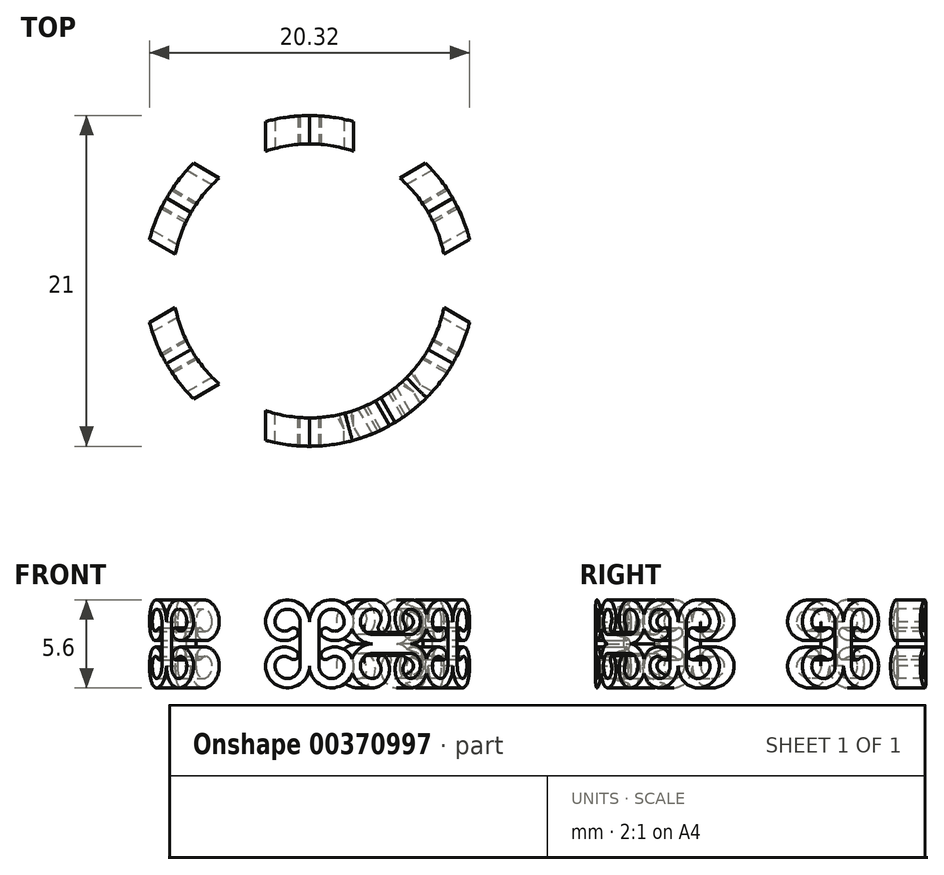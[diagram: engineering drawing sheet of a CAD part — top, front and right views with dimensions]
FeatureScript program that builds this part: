
annotation { "Feature Type Name" : "Feature", "Feature Type Description" : "" }
export const myFeature = defineFeature(function(context is Context, id is Id, definition is map)
    precondition{}
    {
        {
            var Q0;
            Q0=qCreatedBy(makeId("Front.planeOp"),FACE);
            var sketch = newSketch(context, id + "F0", { "sketchPlane" : qUnion([Q0])});
            skLineSegment(sketch, "E0.bottom", {"start": v(0, 0) * mm, "end": v(-2.8, 0) * mm, "construction": true});
            skLineSegment(sketch, "E0.top", {"start": v(0, 2.8) * mm, "end": v(-2.8, 2.8) * mm, "construction": true});
            skLineSegment(sketch, "E0.left", {"start": v(0, 0) * mm, "end": v(0, 2.8) * mm, "construction": true});
            skLineSegment(sketch, "E0.right", {"start": v(-2.8, 0) * mm, "end": v(-2.8, 2.8) * mm, "construction": true});
            skArc(sketch, "E1", {"start": v(0, 1.4) * mm, "mid": v(-1.4, 2.8) * mm, "end": v(-2.8, 1.4) * mm});
            skArc(sketch, "E2", {"start": v(-2.8, 1.4) * mm, "mid": v(-2.1, 0.31) * mm, "end": v(-0.83, 0.48) * mm});
            skLineSegment(sketch, "E3", {"start": v(-1.6, 1.4) * mm, "end": v(-0.83, 0.48) * mm, "construction": true});
            skLineSegment(sketch, "E4", {"start": v(-1.6, 1.4) * mm, "end": v(-1.6, 0.2) * mm, "construction": true});
            skArc(sketch, "E5.0", {"start": v(-2.2, 1.4) * mm, "mid": v(-1.85, 0.86) * mm, "end": v(-1.21, 0.94) * mm});
            skArc(sketch, "E5.1", {"start": v(-0.6, 1.4) * mm, "mid": v(-1.4, 2.2) * mm, "end": v(-2.2, 1.4) * mm});
            skArc(sketch, "E6", {"start": v(-0.83, 0.48) * mm, "mid": v(-0.8, 0.9) * mm, "end": v(-1.21, 0.94) * mm});
            skLineSegment(sketch, "E7", {"start": v(-0.6, 1.4) * mm, "end": v(-0.6, 0) * mm});
            skLineSegment(sketch, "E8", {"start": v(-0.6, 0) * mm, "end": v(0, 0) * mm});
            skLineSegment(sketch, "E9", {"start": v(0, 1.4) * mm, "end": v(0, 0) * mm});
            skLineSegment(sketch, "E10", {"start": v(-0.6, 1.4) * mm, "end": v(0, 1.4) * mm, "construction": true});
            skCircle(sketch, "E11", {"center": v(0, 0) * mm, "radius": 3.33 * mm, "construction": true});
            skSolve(sketch);
        }
        {
            var Q0;
            Q0=makeQuery(id+"F0.imprint","IMPRINT",FACE,{"disambiguationData":[TD([[makeQuery(id+"F0.imprint","IMPRINT",EDGE,{"derivedFrom":sQuery(id+"F0.wireOp",EDGE,"E1")}),1.0]])]});
            extrude(context, id + "F1", {"entities" : qUnion([Q0]), "endBound" : BoundingType.SYMMETRIC, "depth" : 8 * mm});
        }
        {
            var Q0;
            Q0=makeQuery(id+"F1.opExtrude","SWEPT_BODY",BODY,{"disambiguationData":[OSD([sQuery(id+"F0.wireOp",EDGE,"E1"),sQuery(id+"F0.wireOp",EDGE,"E2"),sQuery(id+"F0.wireOp",EDGE,"E5.0"),sQuery(id+"F0.wireOp",EDGE,"E5.1"),sQuery(id+"F0.wireOp",EDGE,"E6"),sQuery(id+"F0.wireOp",EDGE,"E7"),sQuery(id+"F0.wireOp",EDGE,"E8"),sQuery(id+"F0.wireOp",EDGE,"E9")])]});
            var Q1;
            Q1=makeQuery(id+"F1.opExtrude","SWEPT_FACE",FACE,{"disambiguationData":[OSD([sQuery(id+"F0.wireOp",EDGE,"E8")])]});
            mirror(context, id + "F2", {"operationType" : NewBodyOperationType.ADD, "entities" : qUnion([Q0]), "mirrorPlane" : qUnion([Q1])});
        }
        {
            var Q0;
            Q0=makeQuery(id+"F1.opExtrude","SWEPT_BODY",BODY,{"disambiguationData":[OSD([sQuery(id+"F0.wireOp",EDGE,"E1"),sQuery(id+"F0.wireOp",EDGE,"E2"),sQuery(id+"F0.wireOp",EDGE,"E5.0"),sQuery(id+"F0.wireOp",EDGE,"E5.1"),sQuery(id+"F0.wireOp",EDGE,"E6"),sQuery(id+"F0.wireOp",EDGE,"E7"),sQuery(id+"F0.wireOp",EDGE,"E8"),sQuery(id+"F0.wireOp",EDGE,"E9")])]});
            var Q1;
            {var subQ0=makeQuery(id+"F1.opExtrude","SWEPT_FACE",FACE,{"disambiguationData":[OSD([sQuery(id+"F0.wireOp",EDGE,"E9")])]});Q1=makeQuery(id+"F2.boolean.opBoolean","MERGE",FACE,{"derivedFrom":[subQ0,makeQuery(id+"F2.opPattern","COPY",FACE,{"derivedFrom":subQ0,"instanceName":"1"})]});}
            mirror(context, id + "F3", {"operationType" : NewBodyOperationType.ADD, "entities" : qUnion([Q0]), "mirrorPlane" : qUnion([Q1])});
        }
        {
            var Q0;
            Q0=qCreatedBy(makeId("Top.planeOp"),FACE);
            var sketch = newSketch(context, id + "F4", { "sketchPlane" : qUnion([Q0])});
            skCircle(sketch, "E12", {"center": v(0, 8.7) * mm, "radius": 8.7 * mm, "construction": true});
            skSolve(sketch);
        }
        {
            var Q0;
            Q0=makeQuery(id+"F1.opExtrude","SWEPT_BODY",BODY,{"disambiguationData":[OSD([sQuery(id+"F0.wireOp",EDGE,"E1"),sQuery(id+"F0.wireOp",EDGE,"E2"),sQuery(id+"F0.wireOp",EDGE,"E5.0"),sQuery(id+"F0.wireOp",EDGE,"E5.1"),sQuery(id+"F0.wireOp",EDGE,"E6"),sQuery(id+"F0.wireOp",EDGE,"E7"),sQuery(id+"F0.wireOp",EDGE,"E8"),sQuery(id+"F0.wireOp",EDGE,"E9")])]});
            var Q1;
            Q1=sQuery(id+"F0.wireOp",EDGE,"E11");
            transform(context, id + "F5", {"entities" : qUnion([Q0]), "transformType" : TransformType.ROTATION, "transformAxis" : qUnion([Q1]), "angle" : 90 * degree, "makeCopy" : true});
        }
        {
            var Q0;
            Q0=makeQuery(id+"F5.opPattern","COPY",BODY,{"derivedFrom":makeQuery(id+"F1.opExtrude","SWEPT_BODY",BODY,{"disambiguationData":[OSD([sQuery(id+"F0.wireOp",EDGE,"E1"),sQuery(id+"F0.wireOp",EDGE,"E2"),sQuery(id+"F0.wireOp",EDGE,"E5.0"),sQuery(id+"F0.wireOp",EDGE,"E5.1"),sQuery(id+"F0.wireOp",EDGE,"E6"),sQuery(id+"F0.wireOp",EDGE,"E7"),sQuery(id+"F0.wireOp",EDGE,"E8"),sQuery(id+"F0.wireOp",EDGE,"E9")])]}),"instanceName":"1"});
            var Q1;
            Q1=sQuery(id+"F4.wireOp",EDGE,"E12");
            transform(context, id + "F6", {"entities" : qUnion([Q0]), "transformType" : TransformType.ROTATION, "transformAxis" : qUnion([Q1]), "angle" : 30 * degree, "makeCopy" : false});
        }
        {
            var Q0;
            Q0=qCreatedBy(makeId("Top.planeOp"),FACE);
            var sketch = newSketch(context, id + "F7", { "sketchPlane" : qUnion([Q0])});
            skCircle(sketch, "E13.0", {"center": v(0, 8.7) * mm, "radius": 8.7 * mm});
            skCircle(sketch, "E14", {"center": v(0, 8.7) * mm, "radius": 10.5 * mm});
            skCircle(sketch, "E15", {"center": v(0, 8.7) * mm, "radius": 50 * mm});
            skSolve(sketch);
        }
        {
            var Q0;
            Q0=makeQuery(id+"F7.imprint","IMPRINT",FACE,{"disambiguationData":[TD([[makeQuery(id+"F7.imprint","IMPRINT",EDGE,{"derivedFrom":sQuery(id+"F7.wireOp",EDGE,"E14")}),-1.0]])]});
            var Q1;
            Q1=makeQuery(id+"F7.imprint","IMPRINT",FACE,{"disambiguationData":[TD([[makeQuery(id+"F7.imprint","IMPRINT",EDGE,{"derivedFrom":sQuery(id+"F7.wireOp",EDGE,"E13.0")}),1.0]])]});
            var Q2;
            Q2=makeQuery(id+"F7.imprint","IMPRINT",FACE,{"disambiguationData":[TD([[makeQuery(id+"F7.imprint","IMPRINT",EDGE,{"derivedFrom":sQuery(id+"F7.wireOp",EDGE,"E13.0")}),1.0]])]});
            extrude(context, id + "F8", {"entities" : qUnion([Q0, Q1, Q2]), "operationType" : NewBodyOperationType.REMOVE, "endBound" : BoundingType.SYMMETRIC, "oppositeDirection" : true, "depth" : 50 * mm});
        }
        {
            var Q0;
            Q0=makeQuery(id+"F1.opExtrude","SWEPT_BODY",BODY,{"disambiguationData":[OSD([sQuery(id+"F0.wireOp",EDGE,"E1"),sQuery(id+"F0.wireOp",EDGE,"E2"),sQuery(id+"F0.wireOp",EDGE,"E5.0"),sQuery(id+"F0.wireOp",EDGE,"E5.1"),sQuery(id+"F0.wireOp",EDGE,"E6"),sQuery(id+"F0.wireOp",EDGE,"E7"),sQuery(id+"F0.wireOp",EDGE,"E8"),sQuery(id+"F0.wireOp",EDGE,"E9")])]});
            var Q1;
            Q1=sQuery(id+"F4.wireOp",EDGE,"E12");
            circularPattern(context, id + "F9", {"operationType" : NewBodyOperationType.ADD, "entities" : qUnion([Q0]), "axis" : qUnion([Q1]), "angle" : 360 * degree, "instanceCount" : 6, "equalSpace" : true});
        }
    });
